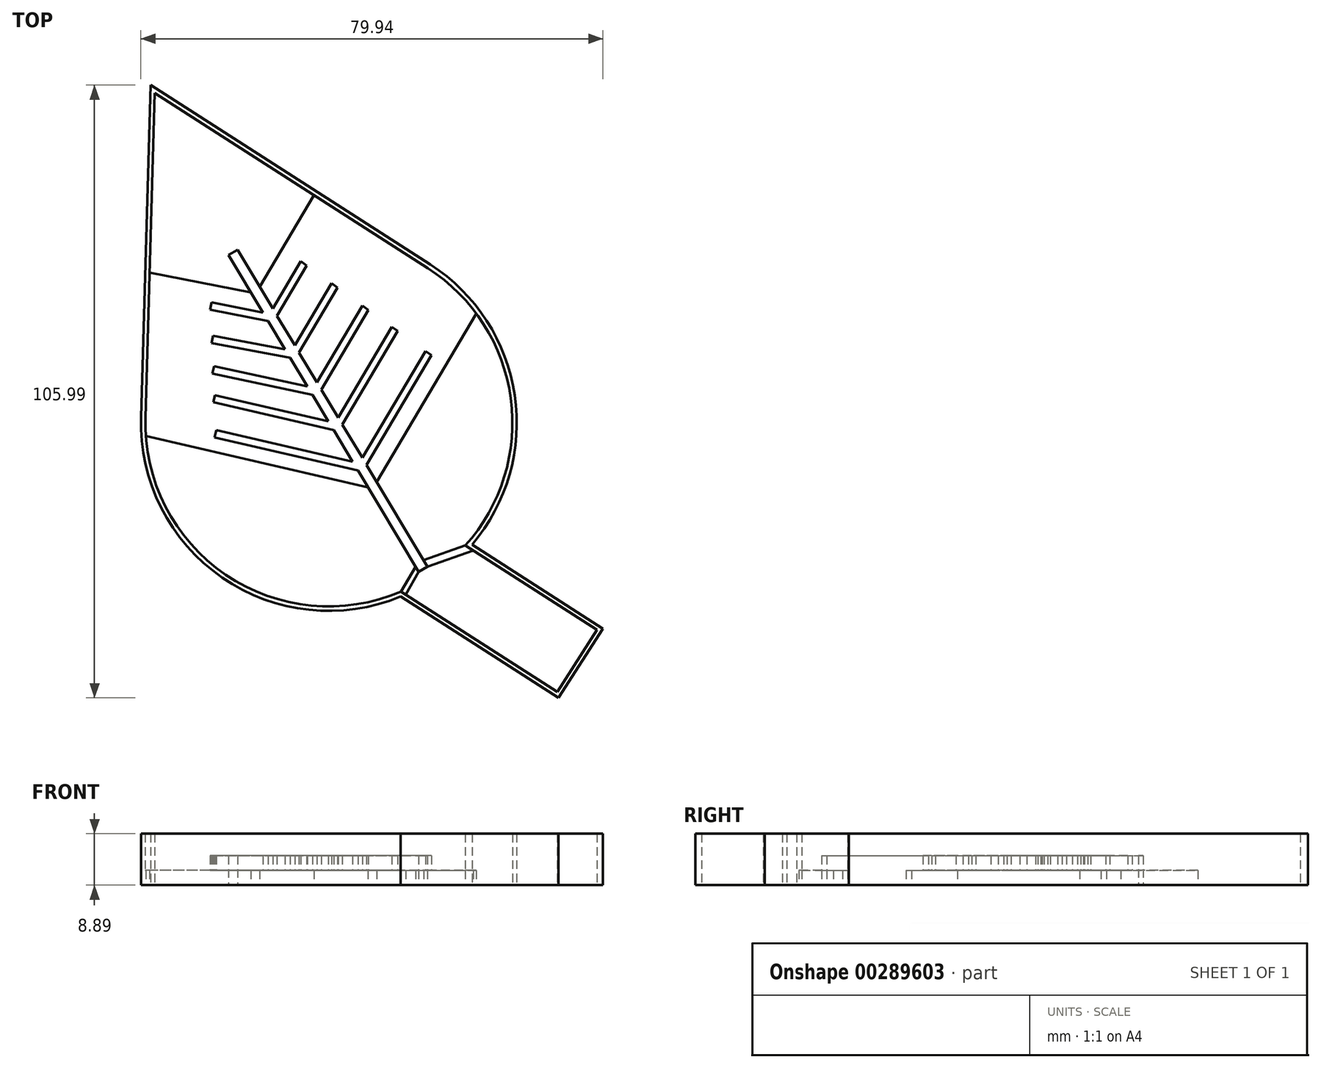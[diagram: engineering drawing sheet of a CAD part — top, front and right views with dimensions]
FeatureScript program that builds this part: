
annotation { "Feature Type Name" : "Feature", "Feature Type Description" : "" }
export const myFeature = defineFeature(function(context is Context, id is Id, definition is map)
    precondition{}
    {
        {
            var Q0;
            Q0=qCreatedBy(makeId("Top.planeOp"),FACE);
            var sketch = newSketch(context, id + "F0", { "sketchPlane" : qUnion([Q0])});
            skPoint(sketch, "E0", {"position": v(-26.34, 56.15) * mm});
            skLineSegment(sketch, "E1", {"start": v(-26.34, 56.15) * mm, "end": v(-27.96, 0.02) * mm});
            skLineSegment(sketch, "E2", {"start": v(-26.34, 56.15) * mm, "end": v(20.92, 25.82) * mm});
            skLineSegment(sketch, "E3", {"start": v(16.27, -30.09) * mm, "end": v(43.29, -47.41) * mm});
            skArc(sketch, "E4.trimOffspring", {"start": v(35.52, -0.9) * mm, "mid": v(31.64, 14.33) * mm, "end": v(20.92, 25.82) * mm});
            skLineSegment(sketch, "E5", {"start": v(7.89, -7.62) * mm, "end": v(-15.7, -2.17) * mm});
            skLineSegment(sketch, "E6", {"start": v(3.7, -0.66) * mm, "end": v(-15.92, 3.88) * mm});
            skLineSegment(sketch, "E7", {"start": v(0.05, 5.42) * mm, "end": v(-16.1, 8.87) * mm});
            skLineSegment(sketch, "E8", {"start": v(-3.79, 11.8) * mm, "end": v(-16.3, 14.16) * mm});
            skLineSegment(sketch, "E9", {"start": v(-7.61, 18.18) * mm, "end": v(-16.5, 19.92) * mm});
            skLineSegment(sketch, "E10", {"start": v(19.33, -26.68) * mm, "end": v(20.86, -25.76) * mm});
            skLineSegment(sketch, "E11", {"start": v(20.86, -25.76) * mm, "end": v(-12.04, 29) * mm});
            skLineSegment(sketch, "E12", {"start": v(19.33, -26.68) * mm, "end": v(-13.6, 28.15) * mm});
            skLineSegment(sketch, "E13.0", {"start": v(4.34, -2.1) * mm, "end": v(-16.2, 2.64) * mm});
            skLineSegment(sketch, "E14.0", {"start": v(0.7, 3.98) * mm, "end": v(-16.36, 7.63) * mm});
            skLineSegment(sketch, "E15.0", {"start": v(-6.95, 16.76) * mm, "end": v(-16.74, 18.67) * mm});
            skLineSegment(sketch, "E16", {"start": v(-15.98, -3.41) * mm, "end": v(-15.7, -2.17) * mm});
            skLineSegment(sketch, "E17", {"start": v(-16.2, 2.64) * mm, "end": v(-15.92, 3.88) * mm});
            skLineSegment(sketch, "E18", {"start": v(-16.36, 7.63) * mm, "end": v(-16.1, 8.87) * mm});
            skLineSegment(sketch, "E19", {"start": v(-16.53, 12.91) * mm, "end": v(-16.3, 14.16) * mm});
            skLineSegment(sketch, "E20", {"start": v(-16.74, 18.67) * mm, "end": v(-16.5, 19.92) * mm});
            skLineSegment(sketch, "E21", {"start": v(-15.98, -3.41) * mm, "end": v(8.8, -9.14) * mm});
            skLineSegment(sketch, "E22", {"start": v(4.34, -2.1) * mm, "end": v(4.61, -2.17) * mm});
            skLineSegment(sketch, "E23", {"start": v(0.7, 3.98) * mm, "end": v(0.95, 3.93) * mm});
            skLineSegment(sketch, "E24", {"start": v(-16.53, 12.91) * mm, "end": v(-2.9, 10.35) * mm});
            skLineSegment(sketch, "E25", {"start": v(-6.95, 16.76) * mm, "end": v(-6.73, 16.71) * mm});
            skLineSegment(sketch, "E26", {"start": v(-12.04, 29) * mm, "end": v(-13.6, 28.15) * mm});
            skArc(sketch, "E27.trimOffspring", {"start": v(-27.96, 0.02) * mm, "mid": v(-14.09, -27.15) * mm, "end": v(16.27, -30.09) * mm});
            skLineSegment(sketch, "E28", {"start": v(21.53, 10.76) * mm, "end": v(20.5, 11.51) * mm});
            skLineSegment(sketch, "E29", {"start": v(-5.94, 18.85) * mm, "end": v(-1.08, 27.05) * mm});
            skLineSegment(sketch, "E30", {"start": v(-0.05, 26.3) * mm, "end": v(-5.2, 17.6) * mm});
            skLineSegment(sketch, "E31", {"start": v(-2.12, 12.5) * mm, "end": v(4.23, 23.22) * mm});
            skLineSegment(sketch, "E32", {"start": v(1.72, 6.1) * mm, "end": v(9.59, 19.36) * mm});
            skLineSegment(sketch, "E33", {"start": v(5.38, 0) * mm, "end": v(14.68, 15.7) * mm});
            skLineSegment(sketch, "E34", {"start": v(9.55, -6.95) * mm, "end": v(20.5, 11.51) * mm});
            skLineSegment(sketch, "E35.trimOffspring", {"start": v(15.71, 14.95) * mm, "end": v(14.68, 15.7) * mm});
            skLineSegment(sketch, "E36.trimOffspring", {"start": v(10.62, 18.62) * mm, "end": v(9.59, 19.36) * mm});
            skLineSegment(sketch, "E37.trimOffspring", {"start": v(5.27, 22.47) * mm, "end": v(4.23, 23.22) * mm});
            skLineSegment(sketch, "E38", {"start": v(5.27, 22.47) * mm, "end": v(-1.38, 11.25) * mm});
            skLineSegment(sketch, "E39", {"start": v(10.62, 18.62) * mm, "end": v(2.46, 4.85) * mm});
            skLineSegment(sketch, "E40", {"start": v(15.71, 14.95) * mm, "end": v(6.12, -1.23) * mm});
            skLineSegment(sketch, "E41", {"start": v(21.53, 10.76) * mm, "end": v(10.3, -8.18) * mm});
            skLineSegment(sketch, "E42", {"start": v(10.64, -7.62) * mm, "end": v(10.63, -7.62) * mm});
            skLineSegment(sketch, "E43.trimOffspring", {"start": v(-0.05, 26.3) * mm, "end": v(-1.08, 27.05) * mm});
            skLineSegment(sketch, "E44", {"start": v(50.14, -36.73) * mm, "end": v(27.38, -22.13) * mm});
            skLineSegment(sketch, "E45", {"start": v(50.14, -36.73) * mm, "end": v(43.29, -47.41) * mm});
            skArc(sketch, "E46.trimOffspring", {"start": v(27.38, -22.13) * mm, "mid": v(33.42, -12.27) * mm, "end": v(35.52, -0.9) * mm});
            skLineSegment(sketch, "E47.0", {"start": v(-27.06, 57.52) * mm, "end": v(21.33, 26.46) * mm});
            skArc(sketch, "E47.1", {"start": v(36.29, -0.9) * mm, "mid": v(32.3, 14.7) * mm, "end": v(21.33, 26.46) * mm});
            skLineSegment(sketch, "E47.2", {"start": v(-27.06, 57.52) * mm, "end": v(-28.72, 0.04) * mm});
            skArc(sketch, "E47.3", {"start": v(28.54, -21.96) * mm, "mid": v(34.29, -12.12) * mm, "end": v(36.29, -0.9) * mm});
            skArc(sketch, "E47.4", {"start": v(-28.72, 0.04) * mm, "mid": v(-14.69, -27.66) * mm, "end": v(16.2, -30.94) * mm});
            skLineSegment(sketch, "E47.5", {"start": v(16.2, -30.94) * mm, "end": v(43.52, -48.47) * mm});
            skLineSegment(sketch, "E47.6", {"start": v(51.2, -36.5) * mm, "end": v(43.52, -48.47) * mm});
            skLineSegment(sketch, "E47.7", {"start": v(51.2, -36.5) * mm, "end": v(28.54, -21.96) * mm});
            skLineSegment(sketch, "E48", {"start": v(10.55, -12.05) * mm, "end": v(-27.9, -3.17) * mm});
            skLineSegment(sketch, "E49", {"start": v(-9.71, 21.67) * mm, "end": v(-27.24, 25.1) * mm});
            skLineSegment(sketch, "E50", {"start": v(-8.2, 22.6) * mm, "end": v(1.2, 38.47) * mm});
            skLineSegment(sketch, "E51", {"start": v(12.04, -11.1) * mm, "end": v(29.29, 18) * mm});
            skLineSegment(sketch, "E52", {"start": v(16.27, -30.09) * mm, "end": v(18.78, -25.76) * mm});
            skLineSegment(sketch, "E53", {"start": v(20.18, -24.64) * mm, "end": v(27.38, -22.13) * mm});
            skLineSegment(sketch, "E54", {"start": v(20.86, -25.76) * mm, "end": v(28.76, -23) * mm});
            skLineSegment(sketch, "E55", {"start": v(19.33, -26.68) * mm, "end": v(17.06, -30.6) * mm});
            skSolve(sketch);
        }
        {
            var Q0;
            {var subQ3=sQuery(id+"F0.wireOp",EDGE,"E1");Q0=makeQuery(id+"F0.imprint","IMPRINT",FACE,{"disambiguationData":[TD([[makeQuery(id+"F0.imprint","IMPRINT",EDGE,{"derivedFrom":subQ3}),-1.0]])]});}
            extrude(context, id + "F1", {"entities" : qUnion([Q0]), "depth" : 8.9 * mm});
        }
        {
            var Q0;
            {var subQ7=sQuery(id+"F0.wireOp",EDGE,"E26");Q0=makeQuery(id+"F0.imprint","IMPRINT",FACE,{"disambiguationData":[TD([[makeQuery(id+"F0.imprint","IMPRINT",EDGE,{"derivedFrom":subQ7}),1.0]])]});}
            var Q1;
            {var subQ0=sQuery(id+"F0.wireOp",EDGE,"E29");Q1=makeQuery(id+"F0.imprint","IMPRINT",FACE,{"disambiguationData":[TD([[makeQuery(id+"F0.imprint","IMPRINT",EDGE,{"derivedFrom":subQ0}),-1.0]])]});}
            var Q2;
            {var subQ0=sQuery(id+"F0.wireOp",EDGE,"E31");Q2=makeQuery(id+"F0.imprint","IMPRINT",FACE,{"disambiguationData":[TD([[makeQuery(id+"F0.imprint","IMPRINT",EDGE,{"derivedFrom":subQ0}),-1.0]])]});}
            var Q3;
            {var subQ0=sQuery(id+"F0.wireOp",EDGE,"E32");Q3=makeQuery(id+"F0.imprint","IMPRINT",FACE,{"disambiguationData":[TD([[makeQuery(id+"F0.imprint","IMPRINT",EDGE,{"derivedFrom":subQ0}),-1.0]])]});}
            var Q4;
            {var subQ0=sQuery(id+"F0.wireOp",EDGE,"E33");Q4=makeQuery(id+"F0.imprint","IMPRINT",FACE,{"disambiguationData":[TD([[makeQuery(id+"F0.imprint","IMPRINT",EDGE,{"derivedFrom":subQ0}),-1.0]])]});}
            var Q5;
            {var subQ1=sQuery(id+"F0.wireOp",EDGE,"E28");Q5=makeQuery(id+"F0.imprint","IMPRINT",FACE,{"disambiguationData":[TD([[makeQuery(id+"F0.imprint","IMPRINT",EDGE,{"derivedFrom":subQ1}),1.0]])]});}
            var Q6;
            {var subQ2=sQuery(id+"F0.wireOp",EDGE,"E9");Q6=makeQuery(id+"F0.imprint","IMPRINT",FACE,{"disambiguationData":[TD([[makeQuery(id+"F0.imprint","IMPRINT",EDGE,{"derivedFrom":subQ2}),1.0]])]});}
            var Q7;
            {var subQ0=sQuery(id+"F0.wireOp",EDGE,"E8");Q7=makeQuery(id+"F0.imprint","IMPRINT",FACE,{"disambiguationData":[TD([[makeQuery(id+"F0.imprint","IMPRINT",EDGE,{"derivedFrom":subQ0}),1.0]])]});}
            var Q8;
            {var subQ1=sQuery(id+"F0.wireOp",EDGE,"E7");Q8=makeQuery(id+"F0.imprint","IMPRINT",FACE,{"disambiguationData":[TD([[makeQuery(id+"F0.imprint","IMPRINT",EDGE,{"derivedFrom":subQ1}),1.0]])]});}
            var Q9;
            {var subQ1=sQuery(id+"F0.wireOp",EDGE,"E6");Q9=makeQuery(id+"F0.imprint","IMPRINT",FACE,{"disambiguationData":[TD([[makeQuery(id+"F0.imprint","IMPRINT",EDGE,{"derivedFrom":subQ1}),1.0]])]});}
            var Q10;
            {var subQ4=sQuery(id+"F0.wireOp",EDGE,"E5");Q10=makeQuery(id+"F0.imprint","IMPRINT",FACE,{"disambiguationData":[TD([[makeQuery(id+"F0.imprint","IMPRINT",EDGE,{"derivedFrom":subQ4}),1.0]])]});}
            extrude(context, id + "F2", {"entities" : qUnion([Q0, Q1, Q2, Q3, Q4, Q5, Q6, Q7, Q8, Q9, Q10]), "depth" : 5.08 * mm});
        }
        {
            var Q0;
            {var subQ16=sQuery(id+"F0.wireOp",EDGE,"E28");Q0=makeQuery(id+"F0.imprint","IMPRINT",FACE,{"disambiguationData":[TD([[makeQuery(id+"F0.imprint","IMPRINT",EDGE,{"derivedFrom":subQ16}),-1.0]])]});}
            var Q1;
            {var subQ13=sQuery(id+"F0.wireOp",EDGE,"E5");Q1=makeQuery(id+"F0.imprint","IMPRINT",FACE,{"disambiguationData":[TD([[makeQuery(id+"F0.imprint","IMPRINT",EDGE,{"derivedFrom":subQ13}),-1.0]])]});}
            var Q2;
            {var subQ2=sQuery(id+"F0.wireOp",EDGE,"E53");Q2=makeQuery(id+"F0.imprint","IMPRINT",FACE,{"disambiguationData":[TD([[makeQuery(id+"F0.imprint","IMPRINT",EDGE,{"derivedFrom":subQ2}),-1.0]])]});}
            var Q3;
            {var subQ0=sQuery(id+"F0.wireOp",EDGE,"E52");Q3=makeQuery(id+"F0.imprint","IMPRINT",FACE,{"disambiguationData":[TD([[makeQuery(id+"F0.imprint","IMPRINT",EDGE,{"derivedFrom":subQ0}),-1.0]])]});}
            extrude(context, id + "F3", {"entities" : qUnion([Q0, Q1, Q2, Q3]), "operationType" : NewBodyOperationType.ADD, "depth" : 2.54 * mm});
        }
    });
